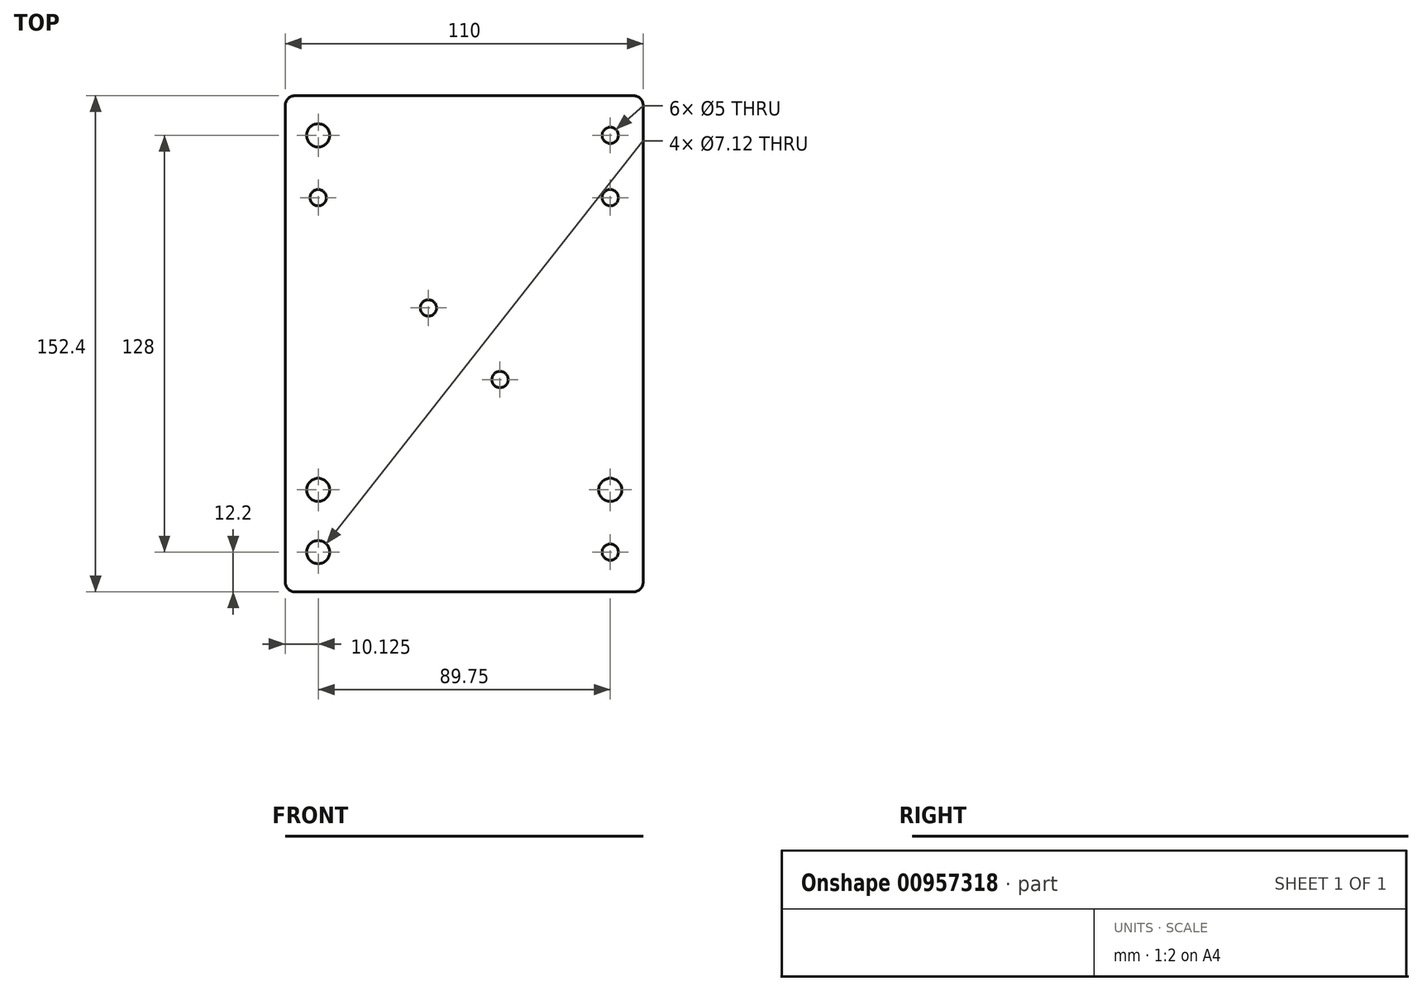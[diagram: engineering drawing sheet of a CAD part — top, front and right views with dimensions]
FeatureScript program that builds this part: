
annotation { "Feature Type Name" : "Feature", "Feature Type Description" : "" }
export const myFeature = defineFeature(function(context is Context, id is Id, definition is map)
    precondition{}
    {
        {
            var Q0;
            Q0=qCreatedBy(makeId("Top.planeOp"),FACE);
            var sketch = newSketch(context, id + "F0", { "sketchPlane" : qUnion([Q0])});
            skCircle(sketch, "E0", {"center": v(-11, 11) * mm, "radius": 2.5 * mm});
            skCircle(sketch, "E1", {"center": v(-44.87, 44.88) * mm, "radius": 2.5 * mm});
            skCircle(sketch, "E2", {"center": v(-44.87, -44.88) * mm, "radius": 3.56 * mm});
            skCircle(sketch, "E3", {"center": v(44.88, 64) * mm, "radius": 2.5 * mm});
            skCircle(sketch, "E4", {"center": v(-44.88, 64) * mm, "radius": 3.56 * mm});
            skLineSegment(sketch, "E5", {"start": v(52, 76.2) * mm, "end": v(-52, 76.2) * mm});
            skArc(sketch, "E6", {"start": v(-52, 76.2) * mm, "mid": v(-54.12, 75.32) * mm, "end": v(-55, 73.2) * mm});
            skLineSegment(sketch, "E7", {"start": v(-55, 73.2) * mm, "end": v(-55, -73.2) * mm});
            skArc(sketch, "E8", {"start": v(-55, -73.2) * mm, "mid": v(-54.12, -75.32) * mm, "end": v(-52, -76.2) * mm});
            skLineSegment(sketch, "E9", {"start": v(-52, -76.2) * mm, "end": v(52, -76.2) * mm});
            skArc(sketch, "E10", {"start": v(52, -76.2) * mm, "mid": v(54.12, -75.32) * mm, "end": v(55, -73.2) * mm});
            skLineSegment(sketch, "E11", {"start": v(55, -73.2) * mm, "end": v(55, 73.2) * mm});
            skArc(sketch, "E12", {"start": v(55, 73.2) * mm, "mid": v(54.12, 75.32) * mm, "end": v(52, 76.2) * mm});
            skCircle(sketch, "E13", {"center": v(-44.87, -64) * mm, "radius": 3.56 * mm});
            skCircle(sketch, "E14", {"center": v(44.88, -64) * mm, "radius": 2.5 * mm});
            skCircle(sketch, "E15", {"center": v(44.88, -44.88) * mm, "radius": 3.56 * mm});
            skCircle(sketch, "E16", {"center": v(44.88, 44.88) * mm, "radius": 2.5 * mm});
            skCircle(sketch, "E17", {"center": v(11, -11) * mm, "radius": 2.5 * mm});
            skLineSegment(sketch, "E18", {"start": v(-44.88, 64) * mm, "end": v(-44.87, 44.88) * mm, "construction": true});
            skLineSegment(sketch, "E19", {"start": v(-44.87, -44.88) * mm, "end": v(-44.87, 44.88) * mm, "construction": true});
            skLineSegment(sketch, "E20", {"start": v(-44.87, -44.88) * mm, "end": v(-44.87, -64) * mm, "construction": true});
            skLineSegment(sketch, "E21", {"start": v(-44.87, -64) * mm, "end": v(-44.87, -76.2) * mm, "construction": true});
            skLineSegment(sketch, "E22", {"start": v(-44.88, 64) * mm, "end": v(-44.88, 76.2) * mm, "construction": true});
            skLineSegment(sketch, "E23", {"start": v(44.88, 44.88) * mm, "end": v(44.88, -44.88) * mm, "construction": true});
            skLineSegment(sketch, "E24", {"start": v(44.88, -64) * mm, "end": v(44.88, -44.88) * mm, "construction": true});
            skLineSegment(sketch, "E25", {"start": v(44.88, -64) * mm, "end": v(44.88, -76.2) * mm, "construction": true});
            skLineSegment(sketch, "E26", {"start": v(-44.87, -64) * mm, "end": v(44.88, -64) * mm, "construction": true});
            skLineSegment(sketch, "E27", {"start": v(44.88, -64) * mm, "end": v(55, -64) * mm, "construction": true});
            skLineSegment(sketch, "E28", {"start": v(-44.87, -64) * mm, "end": v(-55, -64) * mm, "construction": true});
            skLineSegment(sketch, "E29", {"start": v(-44.87, -44.88) * mm, "end": v(-55, -44.88) * mm, "construction": true});
            skLineSegment(sketch, "E30", {"start": v(-44.87, -44.88) * mm, "end": v(44.88, -44.88) * mm, "construction": true});
            skLineSegment(sketch, "E31", {"start": v(44.88, -44.88) * mm, "end": v(55, -44.88) * mm, "construction": true});
            skLineSegment(sketch, "E32", {"start": v(11, -11) * mm, "end": v(55, -11) * mm, "construction": true});
            skLineSegment(sketch, "E33", {"start": v(11, -11) * mm, "end": v(-55, -11) * mm, "construction": true});
            skLineSegment(sketch, "E34", {"start": v(-11, 11) * mm, "end": v(55, 11) * mm, "construction": true});
            skLineSegment(sketch, "E35", {"start": v(-11, 11) * mm, "end": v(-55, 11) * mm, "construction": true});
            skLineSegment(sketch, "E36", {"start": v(-44.87, 44.88) * mm, "end": v(44.88, 44.88) * mm, "construction": true});
            skLineSegment(sketch, "E37", {"start": v(44.88, 44.88) * mm, "end": v(55, 44.88) * mm, "construction": true});
            skLineSegment(sketch, "E38", {"start": v(-44.87, 44.88) * mm, "end": v(-55, 44.87) * mm, "construction": true});
            skLineSegment(sketch, "E39", {"start": v(-44.88, 64) * mm, "end": v(44.88, 64) * mm, "construction": true});
            skLineSegment(sketch, "E40", {"start": v(44.88, 64) * mm, "end": v(55, 64) * mm, "construction": true});
            skLineSegment(sketch, "E41", {"start": v(-44.88, 64) * mm, "end": v(-55, 64) * mm, "construction": true});
            skLineSegment(sketch, "E42", {"start": v(-11, 11) * mm, "end": v(-11, 76.2) * mm, "construction": true});
            skLineSegment(sketch, "E43", {"start": v(-11, 11) * mm, "end": v(-11, -76.2) * mm, "construction": true});
            skLineSegment(sketch, "E44", {"start": v(11, -11) * mm, "end": v(11, -76.2) * mm, "construction": true});
            skLineSegment(sketch, "E45", {"start": v(11, -11) * mm, "end": v(11, 76.2) * mm, "construction": true});
            skLineSegment(sketch, "E46", {"start": v(-11, 11) * mm, "end": v(11, -11) * mm, "construction": true});
            skPoint(sketch, "E47", {"position": v(0, 0) * mm});
            skLineSegment(sketch, "E48", {"start": v(44.88, 64) * mm, "end": v(44.88, 76.2) * mm, "construction": true});
            skLineSegment(sketch, "E49", {"start": v(44.88, 64) * mm, "end": v(44.88, 44.88) * mm, "construction": true});
            skSolve(sketch);
        }
        {
            var Q0;
            Q0=qSketchRegion(id+"F0",true);
            extrude(context, id + "F1", {"entities" : qUnion([Q0]), "depth" : 1 / 203.2 * mm, "offsetDistance" : 25 * mm});
        }
    });
